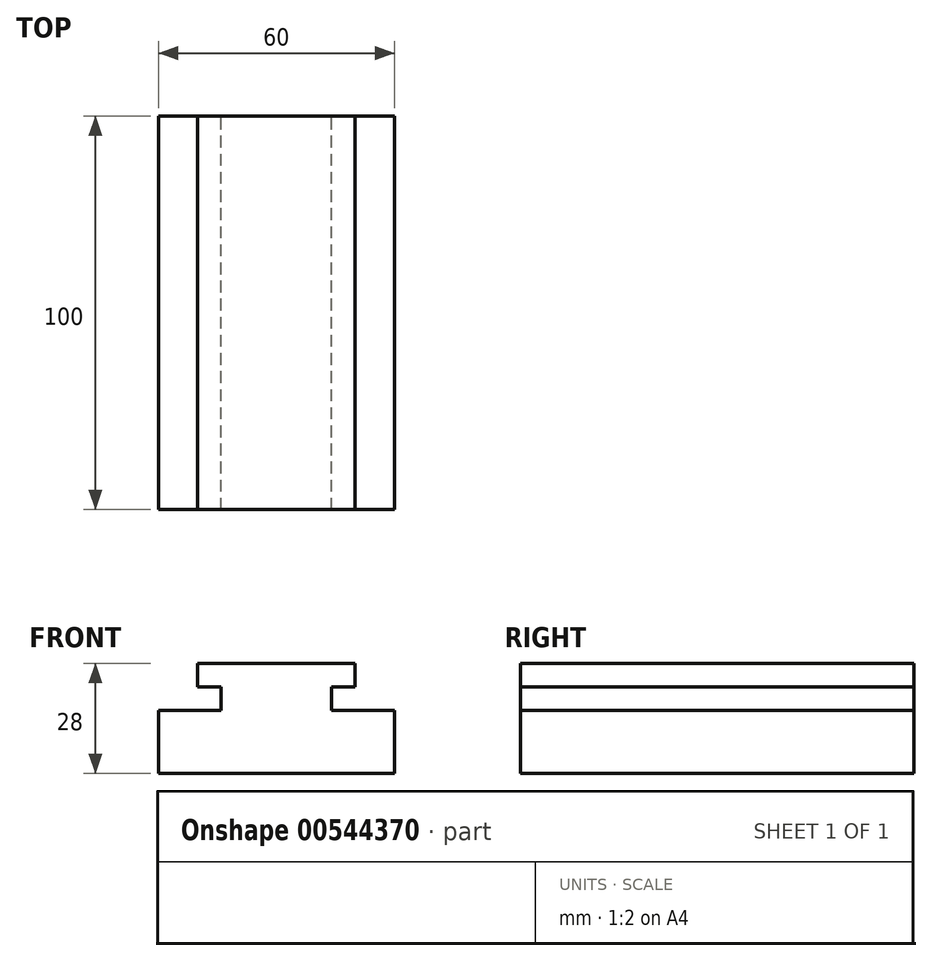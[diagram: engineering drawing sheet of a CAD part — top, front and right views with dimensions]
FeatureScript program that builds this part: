
annotation { "Feature Type Name" : "Feature", "Feature Type Description" : "" }
export const myFeature = defineFeature(function(context is Context, id is Id, definition is map)
    precondition{}
    {
        {
            var Q0;
            Q0=qCreatedBy(makeId("Front.planeOp"),FACE);
            var sketch = newSketch(context, id + "F0", { "sketchPlane" : qUnion([Q0])});
            skLineSegment(sketch, "E0", {"start": v(20, 28) * mm, "end": v(20, 22) * mm});
            skLineSegment(sketch, "E1", {"start": v(14, 22) * mm, "end": v(14, 16) * mm});
            skLineSegment(sketch, "E2", {"start": v(14, 16) * mm, "end": v(30, 16) * mm});
            skLineSegment(sketch, "E3", {"start": v(30, 16) * mm, "end": v(30, 0) * mm});
            skLineSegment(sketch, "E4", {"start": v(30, 0) * mm, "end": v(-30, 0) * mm});
            skLineSegment(sketch, "E5", {"start": v(-30, 0) * mm, "end": v(-30, 16) * mm});
            skLineSegment(sketch, "E6", {"start": v(-30, 16) * mm, "end": v(-14, 16) * mm});
            skLineSegment(sketch, "E7", {"start": v(-14, 16) * mm, "end": v(-14, 22) * mm});
            skLineSegment(sketch, "E8", {"start": v(-20, 28) * mm, "end": v(-20, 22) * mm});
            skLineSegment(sketch, "E9", {"start": v(-20, 22) * mm, "end": v(-14, 22) * mm});
            skLineSegment(sketch, "E10", {"start": v(14, 22) * mm, "end": v(20, 22) * mm});
            skLineSegment(sketch, "E11", {"start": v(20, 28) * mm, "end": v(-20, 28) * mm});
            skSolve(sketch);
        }
        {
            var Q0;
            Q0=makeQuery(id+"F0.imprint","IMPRINT",FACE,{"disambiguationData":[TD([[makeQuery(id+"F0.imprint","IMPRINT",EDGE,{"derivedFrom":sQuery(id+"F0.wireOp",EDGE,"E0")}),-1.0]])]});
            extrude(context, id + "F1", {"entities" : qUnion([Q0]), "endBound" : BoundingType.SYMMETRIC, "depth" : 100 * mm, "offsetDistance" : 25 * mm});
        }
    });
